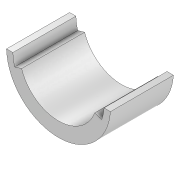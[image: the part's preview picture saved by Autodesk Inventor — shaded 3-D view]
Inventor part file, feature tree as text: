
AUTODESK INVENTOR PART (.ipt)
format: ipt  version: 2020.3 (Build 243373010, 373A)  size: 96,768 bytes
history: native  units: mm
features: extrude x1, sketch x1
ambient origin geometry x8: Origin, YZ Plane, XZ Plane, XY Plane, X Axis, Y Axis, Z Axis, Center Point
bodies: Solid1 (feature_tree)
feature tree (2):
  extrude  "Extrusion1"  [1 undecoded]
  sketch  "Sketch1"  dims[d0=50.0mm d1=0.0mm]
note: 1 required parameter value undecoded (feature->parameter linkage not recoverable at this tier; creation-order binding heuristic only, values carry confidence <= 0.55)
